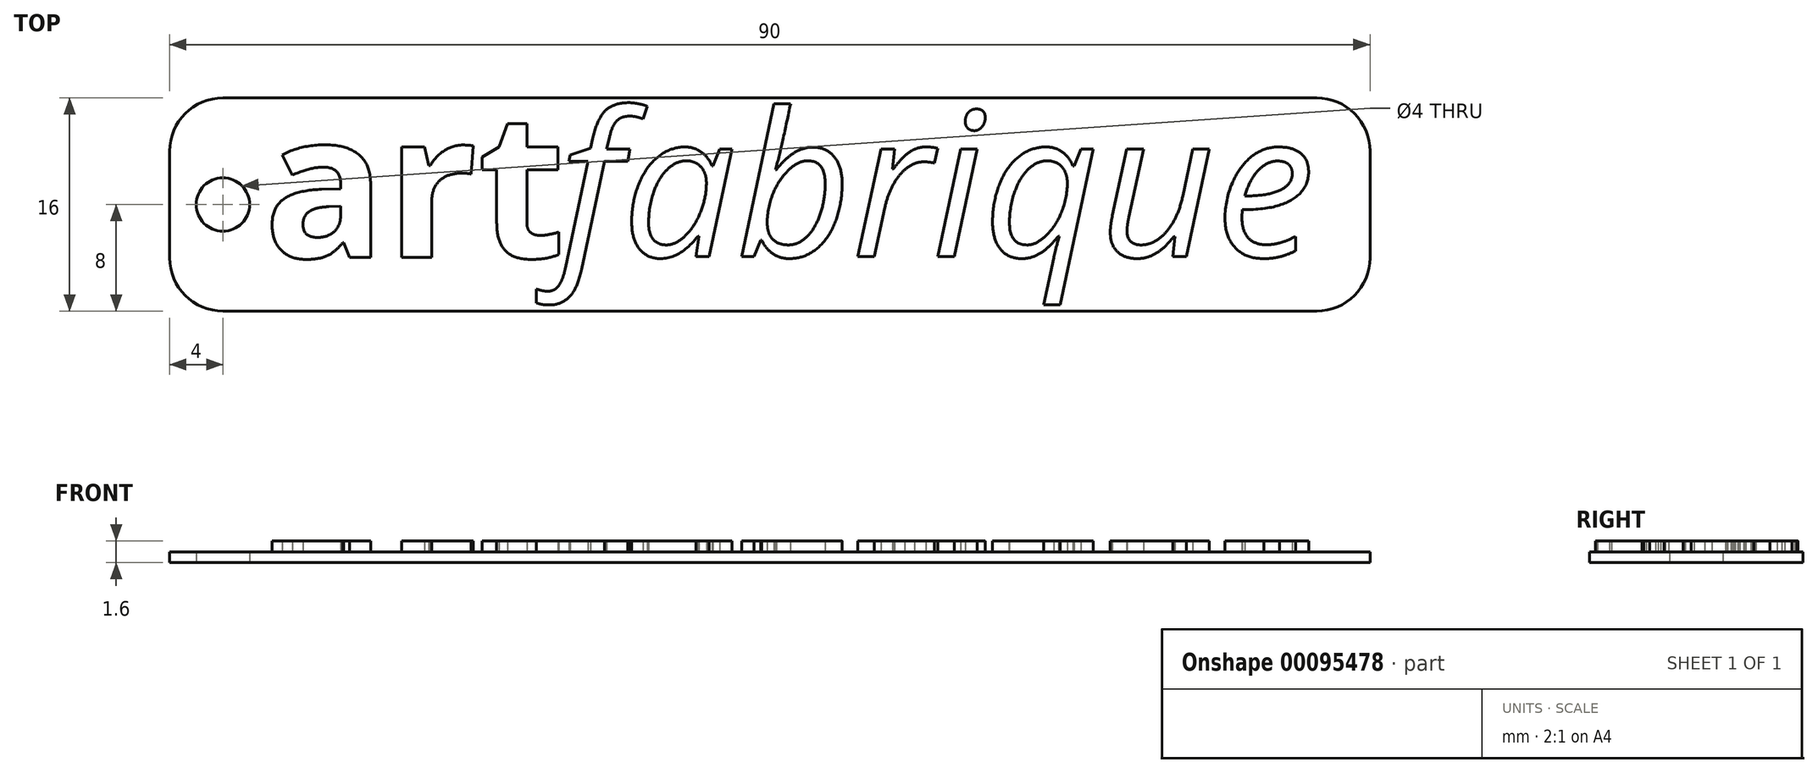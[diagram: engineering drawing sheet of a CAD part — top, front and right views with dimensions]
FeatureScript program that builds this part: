
annotation { "Feature Type Name" : "Feature", "Feature Type Description" : "" }
export const myFeature = defineFeature(function(context is Context, id is Id, definition is map)
    precondition{}
    {
        {
            var Q0;
            Q0=qCreatedBy(makeId("Top.planeOp"),FACE);
            var sketch = newSketch(context, id + "F0", { "sketchPlane" : qUnion([Q0])});
            skLineSegment(sketch, "E0.bottom", {"start": v(0, 16) * mm, "end": v(90, 16) * mm});
            skLineSegment(sketch, "E0.top", {"start": v(0, 0) * mm, "end": v(90, 0) * mm});
            skLineSegment(sketch, "E0.left", {"start": v(0, 16) * mm, "end": v(0, 0) * mm});
            skLineSegment(sketch, "E0.right", {"start": v(90, 16) * mm, "end": v(90, 0) * mm});
            skCircle(sketch, "E1", {"center": v(4, 8) * mm, "radius": 2 * mm});
            skSolve(sketch);
        }
        {
            var Q0;
            Q0=makeQuery(id+"F0.imprint","IMPRINT",FACE,{"disambiguationData":[TD([[makeQuery(id+"F0.imprint","IMPRINT",EDGE,{"derivedFrom":sQuery(id+"F0.wireOp",EDGE,"E0.bottom")}),-1.0]])]});
            extrude(context, id + "F1", {"entities" : qUnion([Q0]), "depth" : 0.8 * mm});
        }
        {
            var Q0;
            Q0=makeQuery(id+"F1.opExtrude","SWEPT_EDGE",EDGE,{"disambiguationData":[OSD([sQuery(id+"F0.wireOp",EDGE,"E0.top"),sQuery(id+"F0.wireOp",EDGE,"E0.right")])]});
            var Q1;
            Q1=makeQuery(id+"F1.opExtrude","SWEPT_EDGE",EDGE,{"disambiguationData":[OSD([sQuery(id+"F0.wireOp",EDGE,"E0.bottom"),sQuery(id+"F0.wireOp",EDGE,"E0.right")])]});
            var Q2;
            Q2=makeQuery(id+"F1.opExtrude","SWEPT_EDGE",EDGE,{"disambiguationData":[OSD([sQuery(id+"F0.wireOp",EDGE,"E0.bottom"),sQuery(id+"F0.wireOp",EDGE,"E0.left")])]});
            var Q3;
            Q3=makeQuery(id+"F1.opExtrude","SWEPT_EDGE",EDGE,{"disambiguationData":[OSD([sQuery(id+"F0.wireOp",EDGE,"E0.top"),sQuery(id+"F0.wireOp",EDGE,"E0.left")])]});
            fillet(context, id + "F2", {"entities" : qUnion([Q0, Q1, Q2, Q3]), "radius" : 4 * mm, "tangentPropagation" : true, "allowEdgeOverflow" : false});
        }
        {
            var Q0;
            Q0=makeQuery(id+"F1.opExtrude","CAP_FACE",FACE,{"disambiguationData":[OSD([sQuery(id+"F0.wireOp",EDGE,"E0.bottom"),sQuery(id+"F0.wireOp",EDGE,"E0.top"),sQuery(id+"F0.wireOp",EDGE,"E0.left"),sQuery(id+"F0.wireOp",EDGE,"E0.right"),sQuery(id+"F0.wireOp",EDGE,"E1")])],"isStart":false});
            var sketch = newSketch(context, id + "F3", { "sketchPlane" : qUnion([Q0])});
            skText(sketch, "E2", { "text": "art", "fontName": "OpenSans-Bold.ttf"});
            skText(sketch, "E3", { "text": "fabrique", "fontName": "OpenSans-Italic.ttf"});
            const initialGuessF3  = {"E2": [0.00705, 0.00403, 1, 0, 0.01092], "E3": [0.0292, 0.00409, 1, 0, 0.01087]};
            skSetInitialGuess(sketch, initialGuessF3);
            skSolve(sketch);
        }
        {
            var Q0;
            Q0 = qSketchRegion(id + "F3", true);
            extrude(context, id + "F4", {"entities" : qUnion([Q0]), "operationType" : NewBodyOperationType.ADD, "depth" : 0.8 * mm});
        }
    });
